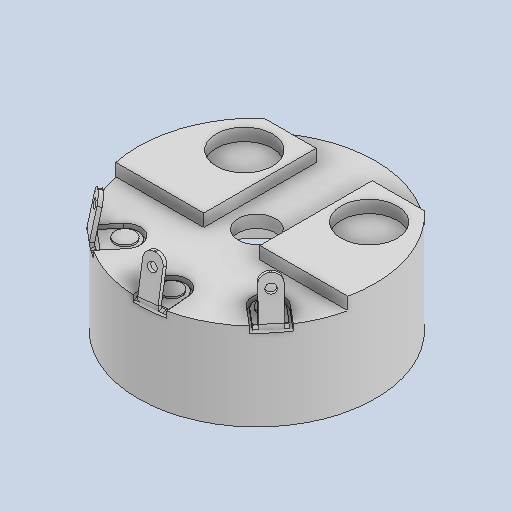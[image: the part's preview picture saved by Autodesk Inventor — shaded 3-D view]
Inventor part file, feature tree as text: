
AUTODESK INVENTOR PART (.ipt)
format: ipt  version: 2025.2 (Build 292293000, 293)  size: 286,208 bytes
history: native  units: mm
features: other x8, revolve x2, sketch x1, pattern_circular x1
ambient origin geometry x8: Origin, YZ Plane, XZ Plane, XY Plane, X Axis, Y Axis, Z Axis, Center Point
bodies: Body1 (feature_tree), Body2 (feature_tree), Body3 (feature_tree), Body4 (feature_tree), Body5 (feature_tree), Body6 (feature_tree)
feature tree (12):
  other  "Bryła1"
  other  "Bryła2"
  other  "Bryła3"
  other  "Bryła4"
  other  "Bryła5"
  other  "Bryła6"
  revolve  "Revolve1[1]"  [1 undecoded]
  revolve  "Revolve1[2]"  [1 undecoded]
  other  "CirPattern3[1]"
  other  "CirPattern3[2]"
  sketch  "Sketched Bend19"
  pattern_circular  "CirPattern4"
note: 2 required parameter values undecoded (feature->parameter linkage not recoverable at this tier; creation-order binding heuristic only, values carry confidence <= 0.55)
